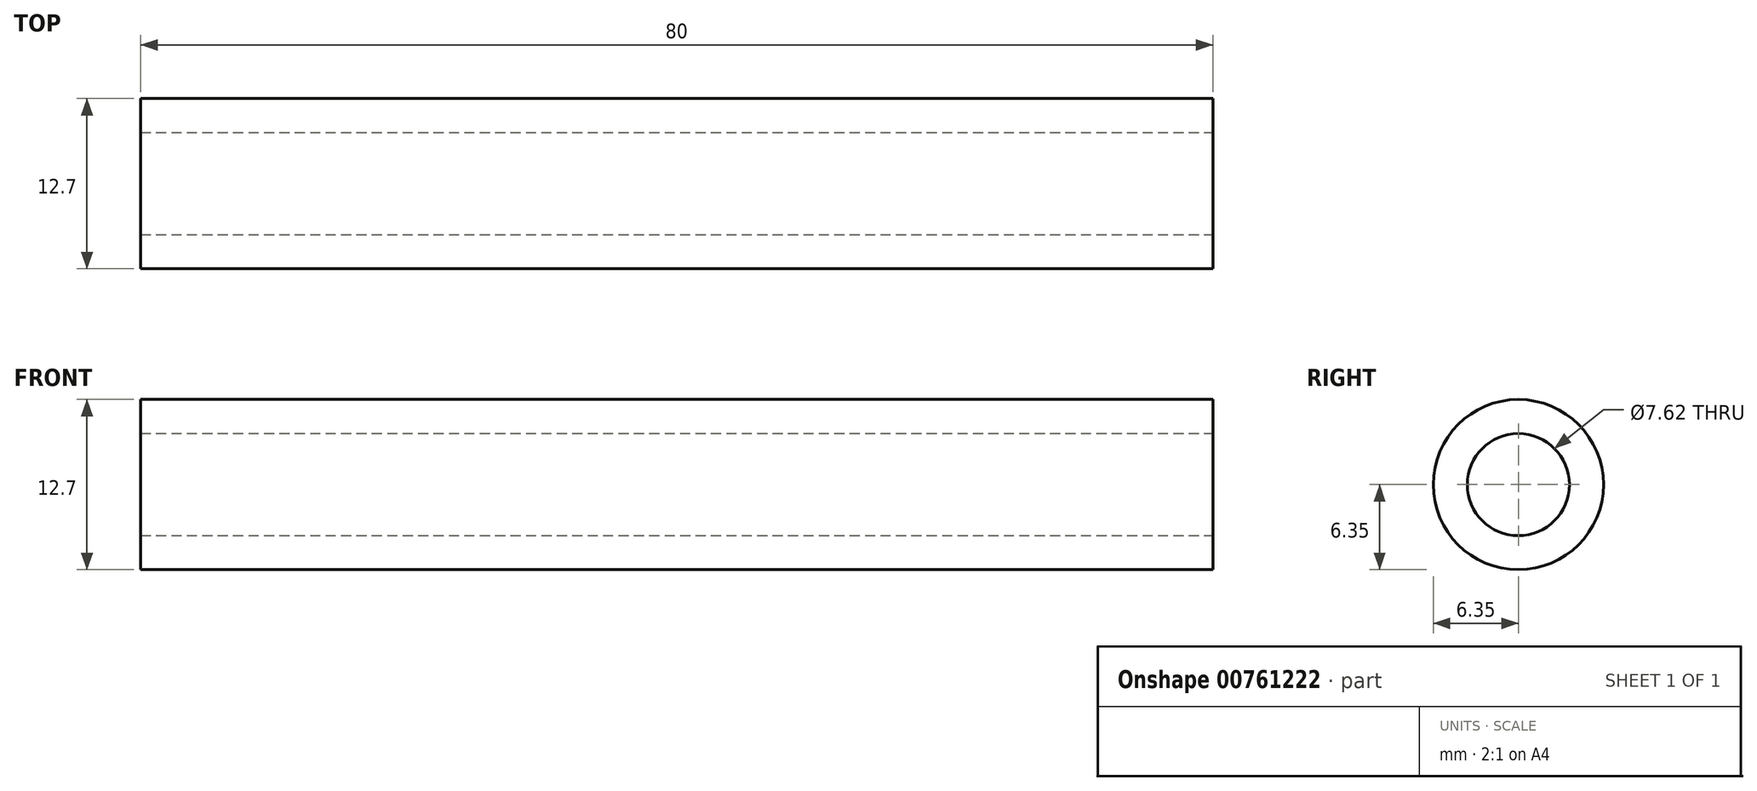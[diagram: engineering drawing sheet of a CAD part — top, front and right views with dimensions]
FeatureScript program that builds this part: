
annotation { "Feature Type Name" : "Feature", "Feature Type Description" : "" }
export const myFeature = defineFeature(function(context is Context, id is Id, definition is map)
    precondition{}
    {
        {
            var Q0;
            Q0=qCreatedBy(makeId("Front.planeOp"),FACE);
            var sketch = newSketch(context, id + "F0", { "sketchPlane" : qUnion([Q0]), "disableImprinting" : false});
            skLineSegment(sketch, "E0", {"start": v(0, 3.8) * mm, "end": v(-80, 3.8) * mm});
            skLineSegment(sketch, "E1", {"start": v(-80, 3.8) * mm, "end": v(-80, 6.35) * mm});
            skLineSegment(sketch, "E2", {"start": v(-80, 6.35) * mm, "end": v(0, 6.35) * mm});
            skLineSegment(sketch, "E3", {"start": v(0, 6.35) * mm, "end": v(0, 3.8) * mm});
            skLineSegment(sketch, "E4", {"start": v(0, 0) * mm, "end": v(-80, 0) * mm, "construction": true});
            skSolve(sketch);
        }
        {
            var Q0;
            Q0=makeQuery(id+"F0.imprint","IMPRINT",FACE,{"disambiguationData":[TD([[makeQuery(id+"F0.imprint","IMPRINT",EDGE,{"derivedFrom":sQuery(id+"F0.wireOp",EDGE,"E0")}),-1.0]])]});
            var Q1;
            Q1=sQuery(id+"F0.wireOp",EDGE,"E1");
            var Q2;
            Q2=sQuery(id+"F0.wireOp",EDGE,"E2");
            var Q3;
            Q3=sQuery(id+"F0.wireOp",EDGE,"E3");
            var Q4;
            Q4=sQuery(id+"F0.wireOp",EDGE,"E0");
            var Q5;
            Q5=sQuery(id+"F0.wireOp",EDGE,"E4");
            revolve(context, id + "F1", {"surfaceOperationType" : NewSurfaceOperationType.NEW, "entities" : qUnion([Q0]), "surfaceEntities" : qUnion([Q1, Q2, Q3, Q4]), "axis" : qUnion([Q5]), "revolveType" : RevolveType.FULL});
        }
    });
